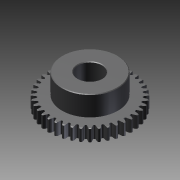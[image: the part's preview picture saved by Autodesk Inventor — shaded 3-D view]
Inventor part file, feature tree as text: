
AUTODESK INVENTOR PART (.ipt)
format: ipt  version: 2011 SP1 (Build 150282100, 282)  size: 1,196,032 bytes
history: native  units: mm
features: other x14, revolve x3, sketch x3, extrude x1, hole x1
ambient origin geometry x8: Origin, YZ Plane, XZ Plane, XY Plane, X Axis, Y Axis, Z Axis, Center Point
bodies: Solid1 (feature_tree)
feature tree (22):
  revolve  "Revolution1"  [1 undecoded]
  extrude  "Extrusion1"  TaperAngle=360.0deg  [1 undecoded]
  hole  "Hole1"  [1 undecoded]
  revolve  "Revolution2"  [1 undecoded]
  revolve  "Revolution3"  [1 undecoded]
  other  "b_XY"
  other  "b_YZ"
  other  "b_ZX"
  other  "b_X"
  other  "b_Y"
  other  "b_Z"
  other  "b_Center"
  other  "turn_around_XY"
  other  "turn_around_YZ"
  other  "turn_around_ZX"
  other  "turn_around_X"
  other  "turn_around_Y"
  other  "turn_around_Z"
  other  "turn_around_Center"
  sketch  "Sketch_2"  dims[d0=360.0deg d1=6.0mm d2=0.0mm]
  sketch  "Sketch_3"  dims[d3=12.0mm d4=6.0mm d5=4.0mm d6=2.0mm d7=90.0deg d8=16.0mm d9=0.0mm d10=360.0deg]
  sketch  "Sketch3"  dims[d11=360.0deg d12=0.0mm]
note: 5 required parameter values undecoded (feature->parameter linkage not recoverable at this tier; creation-order binding heuristic only, values carry confidence <= 0.55)